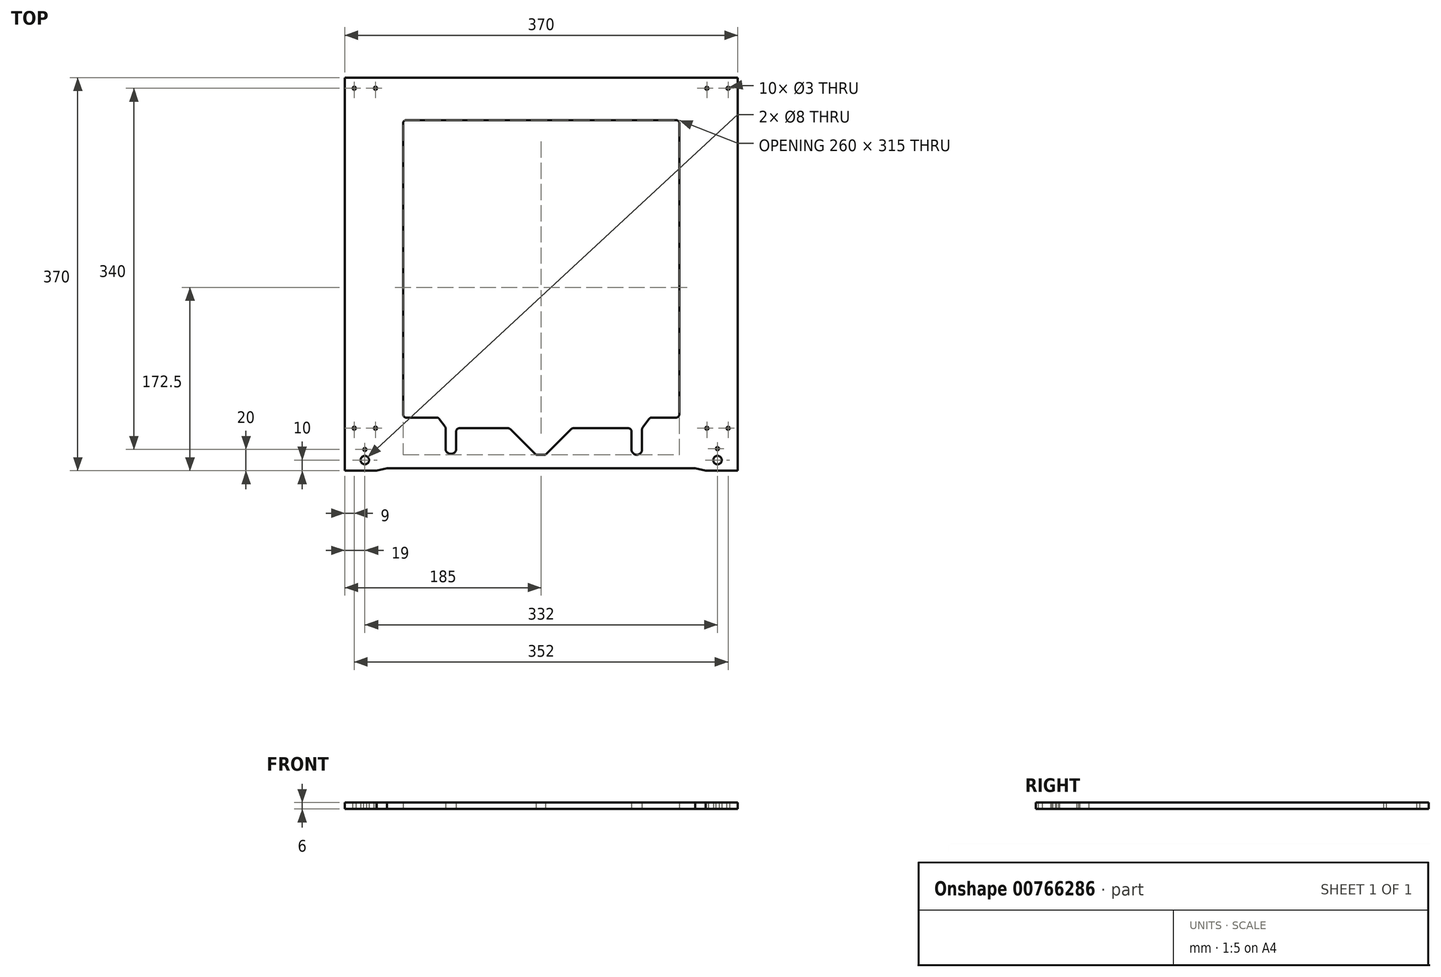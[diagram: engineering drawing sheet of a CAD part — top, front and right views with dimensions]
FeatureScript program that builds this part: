
annotation { "Feature Type Name" : "Feature", "Feature Type Description" : "" }
export const myFeature = defineFeature(function(context is Context, id is Id, definition is map)
    precondition{}
    {
        {
            var Q0;
            Q0=qCreatedBy(makeId("Top.planeOp"),FACE);
            var sketch = newSketch(context, id + "F0", { "sketchPlane" : qUnion([Q0])});
            skLineSegment(sketch, "E0.bottom", {"start": v(-185, 185) * mm, "end": v(185, 185) * mm});
            skLineSegment(sketch, "E0.left", {"start": v(-185, 185) * mm, "end": v(-185, -185) * mm});
            skLineSegment(sketch, "E0.right", {"start": v(185, 185) * mm, "end": v(185, -185) * mm});
            skPoint(sketch, "E0.middle", {"position": v(0, 0) * mm});
            skLineSegment(sketch, "E1.bottom", {"start": v(-127.02, 145) * mm, "end": v(127.02, 145) * mm});
            skLineSegment(sketch, "E2.left", {"start": v(95, -165) * mm, "end": v(95, -146) * mm});
            skLineSegment(sketch, "E2.right", {"start": v(85, -165) * mm, "end": v(85, -148) * mm});
            skLineSegment(sketch, "E3.bottom", {"start": v(-0.5, -170) * mm, "end": v(-5, -169.97) * mm});
            skLineSegment(sketch, "E4.bottom", {"start": v(-0.5, -170) * mm, "end": v(4, -170) * mm});
            skLineSegment(sketch, "E5", {"start": v(4, -170) * mm, "end": v(28.12, -145.88) * mm});
            skLineSegment(sketch, "E6", {"start": v(-5, -169.97) * mm, "end": v(-29.12, -145.88) * mm});
            skLineSegment(sketch, "E7", {"start": v(82, -145) * mm, "end": v(30.24, -145) * mm});
            skLineSegment(sketch, "E8", {"start": v(-31.24, -145) * mm, "end": v(-77, -145) * mm});
            skLineSegment(sketch, "E9", {"start": v(-80, -148) * mm, "end": v(-80, -164.2) * mm});
            skLineSegment(sketch, "E10", {"start": v(-90, -145.2) * mm, "end": v(-90, -164.2) * mm});
            skArc(sketch, "E11", {"start": v(85, -165) * mm, "mid": v(90, -170) * mm, "end": v(95, -165) * mm});
            skArc(sketch, "E12", {"start": v(-90, -164.2) * mm, "mid": v(-85, -169.2) * mm, "end": v(-80, -164.2) * mm});
            skPoint(sketch, "E13.visualSharp", {"position": v(-130, 145) * mm});
            skArc(sketch, "E13.filletArc", {"start": v(-127.02, 145) * mm, "mid": v(-129.01, 144.24) * mm, "end": v(-130, 142.35) * mm});
            skPoint(sketch, "E14.visualSharp", {"position": v(130, 145) * mm});
            skArc(sketch, "E14.filletArc", {"start": v(130, 142.35) * mm, "mid": v(129.01, 144.24) * mm, "end": v(127.02, 145) * mm});
            skLineSegment(sketch, "E15", {"start": v(-155, -185) * mm, "end": v(-185, -185) * mm});
            skLineSegment(sketch, "E16", {"start": v(185, -185) * mm, "end": v(155, -185) * mm});
            skCircle(sketch, "E17", {"center": v(-176, 175) * mm, "radius": 1.5 * mm});
            skCircle(sketch, "E18", {"center": v(-156, 175) * mm, "radius": 1.5 * mm});
            skCircle(sketch, "E19", {"center": v(176, 175) * mm, "radius": 1.5 * mm});
            skCircle(sketch, "E20", {"center": v(156, 175) * mm, "radius": 1.5 * mm});
            skLineSegment(sketch, "E21", {"start": v(127, -135) * mm, "end": v(104, -135) * mm});
            skLineSegment(sketch, "E22", {"start": v(101.6, -136.2) * mm, "end": v(95.6, -144.2) * mm});
            skLineSegment(sketch, "E23", {"start": v(130, 142.35) * mm, "end": v(130, -132) * mm});
            skLineSegment(sketch, "E24", {"start": v(-127, -135) * mm, "end": v(-98.4, -135) * mm});
            skLineSegment(sketch, "E25", {"start": v(-130, -132) * mm, "end": v(-130, 142.35) * mm});
            skLineSegment(sketch, "E26", {"start": v(-90.6, -143.4) * mm, "end": v(-96, -136.2) * mm});
            skPoint(sketch, "E27.visualSharp", {"position": v(-96.9, -135) * mm});
            skArc(sketch, "E27.filletArc", {"start": v(-96, -136.2) * mm, "mid": v(-97.06, -135.32) * mm, "end": v(-98.4, -135) * mm});
            skPoint(sketch, "E28.visualSharp", {"position": v(-130, -135) * mm});
            skArc(sketch, "E28.filletArc", {"start": v(-130, -132) * mm, "mid": v(-129.12, -134.12) * mm, "end": v(-127, -135) * mm});
            skPoint(sketch, "E29.visualSharp", {"position": v(-90, -144.2) * mm});
            skArc(sketch, "E29.filletArc", {"start": v(-90, -145.2) * mm, "mid": v(-90.15, -144.25) * mm, "end": v(-90.6, -143.4) * mm});
            skPoint(sketch, "E30.visualSharp", {"position": v(-80, -145) * mm});
            skArc(sketch, "E30.filletArc", {"start": v(-77, -145) * mm, "mid": v(-79.12, -145.88) * mm, "end": v(-80, -148) * mm});
            skPoint(sketch, "E31.visualSharp", {"position": v(-30, -145) * mm});
            skArc(sketch, "E31.filletArc", {"start": v(-29.12, -145.88) * mm, "mid": v(-30.1, -145.23) * mm, "end": v(-31.24, -145) * mm});
            skPoint(sketch, "E32.visualSharp", {"position": v(29, -145) * mm});
            skArc(sketch, "E32.filletArc", {"start": v(30.24, -145) * mm, "mid": v(29.1, -145.23) * mm, "end": v(28.12, -145.88) * mm});
            skPoint(sketch, "E33.visualSharp", {"position": v(85, -145) * mm});
            skArc(sketch, "E33.filletArc", {"start": v(85, -148) * mm, "mid": v(84.12, -145.88) * mm, "end": v(82, -145) * mm});
            skPoint(sketch, "E34.visualSharp", {"position": v(95, -145) * mm});
            skArc(sketch, "E34.filletArc", {"start": v(95.6, -144.2) * mm, "mid": v(95.15, -145.05) * mm, "end": v(95, -146) * mm});
            skPoint(sketch, "E35.visualSharp", {"position": v(102.5, -135) * mm});
            skArc(sketch, "E35.filletArc", {"start": v(104, -135) * mm, "mid": v(102.66, -135.32) * mm, "end": v(101.6, -136.2) * mm});
            skPoint(sketch, "E36.visualSharp", {"position": v(130, -135) * mm});
            skArc(sketch, "E36.filletArc", {"start": v(127, -135) * mm, "mid": v(129.12, -134.12) * mm, "end": v(130, -132) * mm});
            skCircle(sketch, "E37", {"center": v(-166, -175) * mm, "radius": 4 * mm});
            skLineSegment(sketch, "E38", {"start": v(-155, -185) * mm, "end": v(-145.34, -182.65) * mm});
            skLineSegment(sketch, "E39", {"start": v(155, -185) * mm, "end": v(145.15, -182.65) * mm});
            skLineSegment(sketch, "E40", {"start": v(145.15, -182.65) * mm, "end": v(-145.34, -182.65) * mm});
            skCircle(sketch, "E41", {"center": v(-166, -165) * mm, "radius": 1.5 * mm});
            skCircle(sketch, "E42", {"center": v(-176, -145) * mm, "radius": 1.5 * mm});
            skCircle(sketch, "E43", {"center": v(-156, -145) * mm, "radius": 1.5 * mm});
            skCircle(sketch, "E44", {"center": v(166, -175) * mm, "radius": 4 * mm});
            skCircle(sketch, "E45", {"center": v(176, -145) * mm, "radius": 1.5 * mm});
            skCircle(sketch, "E46", {"center": v(166, -164.2) * mm, "radius": 1.5 * mm});
            skCircle(sketch, "E47", {"center": v(156, -145) * mm, "radius": 1.5 * mm});
            skSolve(sketch);
        }
        {
            var Q0;
            Q0=makeQuery(id+"F0.imprint","IMPRINT",FACE,{"disambiguationData":[TD([[makeQuery(id+"F0.imprint","IMPRINT",EDGE,{"derivedFrom":sQuery(id+"F0.wireOp",EDGE,"E0.bottom")}),-1.0]])]});
            extrude(context, id + "F1", {"entities" : qUnion([Q0]), "depth" : 6 * mm, "offsetDistance" : 25 * mm});
        }
    });
